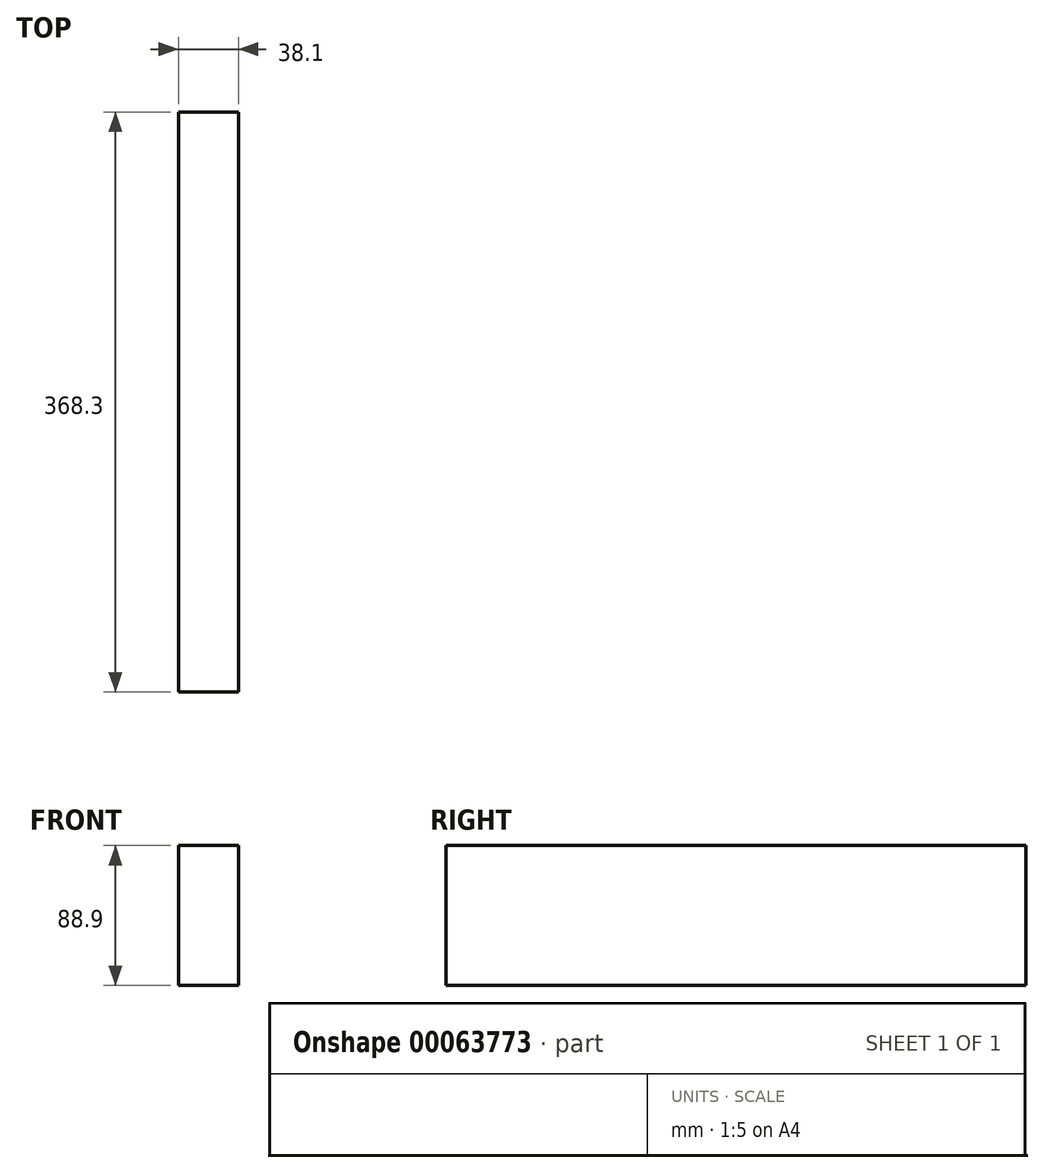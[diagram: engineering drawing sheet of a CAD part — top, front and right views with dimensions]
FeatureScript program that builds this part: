
annotation { "Feature Type Name" : "Feature", "Feature Type Description" : "" }
export const myFeature = defineFeature(function(context is Context, id is Id, definition is map)
    precondition{}
    {
        {
            var Q0;
            Q0=qCreatedBy(makeId("Front.planeOp"),FACE);
            var sketch = newSketch(context, id + "F0", { "sketchPlane" : qUnion([Q0])});
            skLineSegment(sketch, "E0.bottom", {"start": v(-18, 55.77) * mm, "end": v(20.1, 55.77) * mm});
            skLineSegment(sketch, "E0.top", {"start": v(-18, -33.13) * mm, "end": v(20.1, -33.13) * mm});
            skLineSegment(sketch, "E0.left", {"start": v(-18, 55.77) * mm, "end": v(-18, -33.13) * mm});
            skLineSegment(sketch, "E0.right", {"start": v(20.1, 55.77) * mm, "end": v(20.1, -33.13) * mm});
            skSolve(sketch);
        }
        {
            var Q0;
            Q0=qSketchRegion(id+"F0",true);
            extrude(context, id + "F1", {"entities" : qUnion([Q0]), "endBound" : BoundingType.SYMMETRIC, "depth" : 368.3 * mm});
        }
    });
